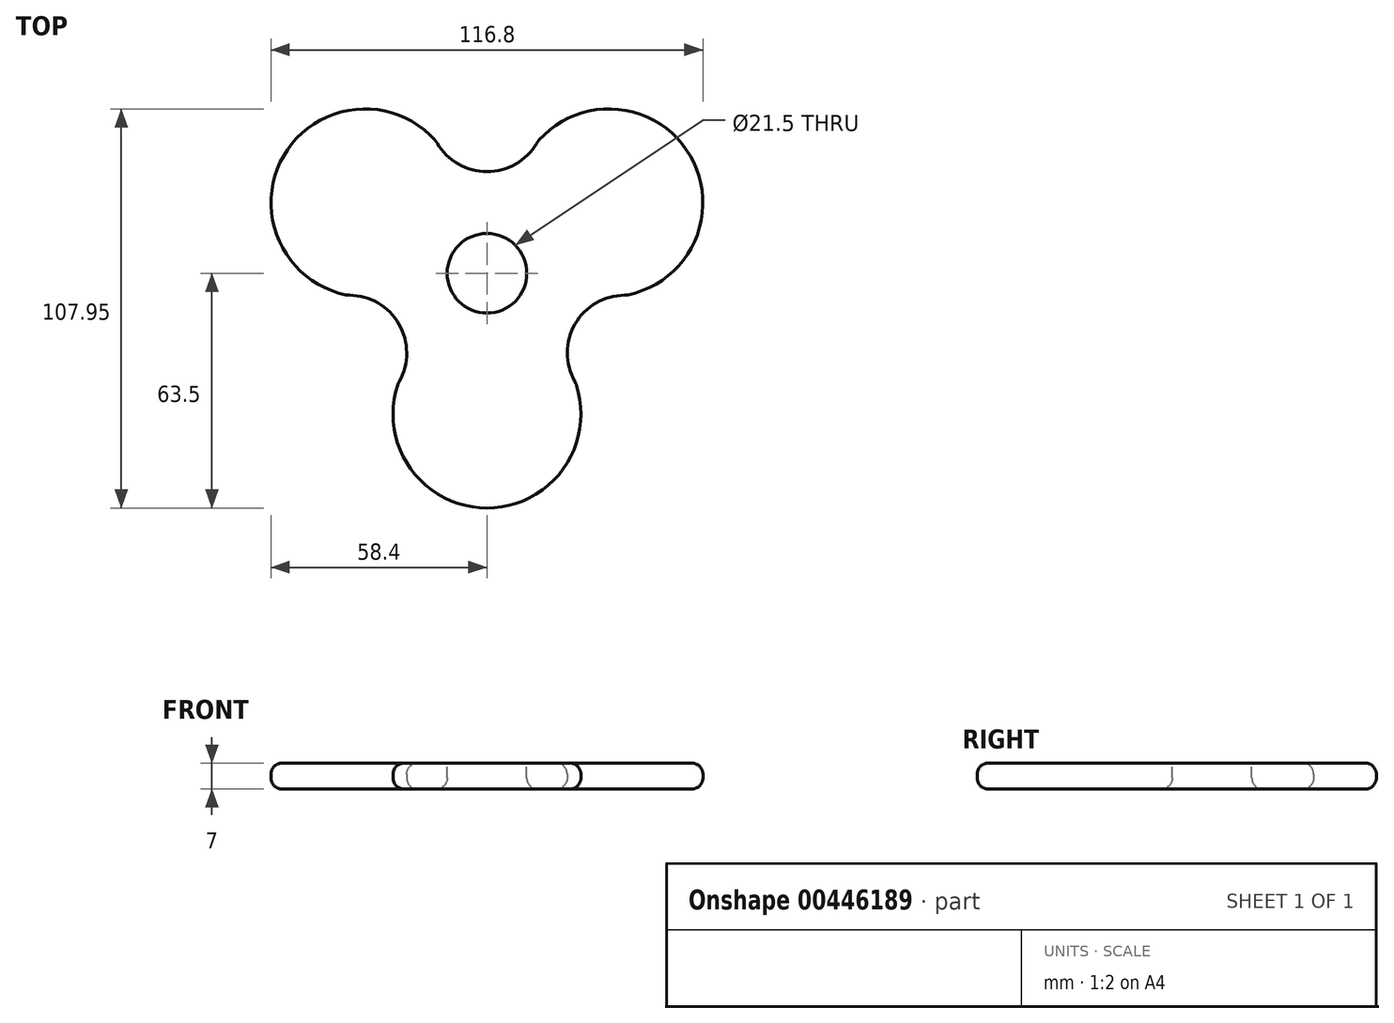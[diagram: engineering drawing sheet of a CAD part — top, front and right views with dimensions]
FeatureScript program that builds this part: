
annotation { "Feature Type Name" : "Feature", "Feature Type Description" : "" }
export const myFeature = defineFeature(function(context is Context, id is Id, definition is map)
    precondition{}
    {
        {
            var Q0;
            Q0=qCreatedBy(makeId("Top.planeOp"),FACE);
            var sketch = newSketch(context, id + "F0", { "sketchPlane" : qUnion([Q0])});
            skCircle(sketch, "E0", {"center": v(0, 0) * mm, "radius": 38.1 * mm});
            skCircle(sketch, "E1", {"center": v(0, -38.1) * mm, "radius": 25.4 * mm});
            skCircle(sketch, "E2", {"center": v(-33, 19.05) * mm, "radius": 25.4 * mm});
            skCircle(sketch, "E3", {"center": v(33, 19.05) * mm, "radius": 25.4 * mm});
            skArc(sketch, "E4", {"start": v(-23.95, -29.63) * mm, "mid": v(-23.81, -13.75) * mm, "end": v(-37.64, -5.93) * mm});
            skArc(sketch, "E5", {"start": v(37.64, -5.93) * mm, "mid": v(23.81, -13.75) * mm, "end": v(23.95, -29.63) * mm});
            skArc(sketch, "E6", {"start": v(-13.7, 35.55) * mm, "mid": v(0, 27.49) * mm, "end": v(13.7, 35.55) * mm});
            skSolve(sketch);
        }
        {
            var Q0;
            {var subQ1=sQuery(id+"F0.wireOp",EDGE,"E1");var subQ8=sQuery(id+"F0.wireOp",EDGE,"E5");var subQ11=makeQuery(id+"F0.imprint","INTERSECT",VERTEX,{"derivedFrom":[subQ1,subQ8]});Q0=makeQuery(id+"F0.imprint","IMPRINT",FACE,{"disambiguationData":[TD([[makeQuery(id+"F0.imprint","IMPRINT",EDGE,{"disambiguationData":[TD([[subQ11,-1.0]])],"derivedFrom":subQ1}),-1.0]])]});}
            var Q1;
            {var subQ1=sQuery(id+"F0.wireOp",EDGE,"E1");var subQ4=sQuery(id+"F0.wireOp",EDGE,"E5");var subQ7=makeQuery(id+"F0.imprint","INTERSECT",VERTEX,{"derivedFrom":[subQ1,subQ4]});Q1=makeQuery(id+"F0.imprint","IMPRINT",FACE,{"disambiguationData":[TD([[makeQuery(id+"F0.imprint","IMPRINT",EDGE,{"disambiguationData":[TD([[subQ7,-1.0]])],"derivedFrom":subQ1}),1.0]])]});}
            var Q2;
            {var subQ0=sQuery(id+"F0.wireOp",EDGE,"E1");var subQ1=sQuery(id+"F0.wireOp",EDGE,"E0");var subQ2=makeQuery(id+"F0.imprint","INTERSECT",VERTEX,{"derivedFrom":[subQ1,subQ0,sQuery(id+"F0.wireOp",EDGE,"E4")]});Q2=makeQuery(id+"F0.imprint","IMPRINT",FACE,{"disambiguationData":[TD([[makeQuery(id+"F0.imprint","IMPRINT",EDGE,{"disambiguationData":[TD([[subQ2,-1.0]])],"derivedFrom":subQ1}),-1.0]])]});}
            var Q3;
            {var subQ1=sQuery(id+"F0.wireOp",EDGE,"E3");var subQ4=sQuery(id+"F0.wireOp",EDGE,"E6");var subQ6=makeQuery(id+"F0.imprint","INTERSECT",VERTEX,{"derivedFrom":[subQ1,subQ4]});Q3=makeQuery(id+"F0.imprint","IMPRINT",FACE,{"disambiguationData":[TD([[makeQuery(id+"F0.imprint","IMPRINT",EDGE,{"disambiguationData":[TD([[subQ6,-1.0]])],"derivedFrom":subQ1}),1.0]])]});}
            var Q4;
            {var subQ0=sQuery(id+"F0.wireOp",EDGE,"E3");var subQ1=sQuery(id+"F0.wireOp",EDGE,"E0");var subQ2=makeQuery(id+"F0.imprint","INTERSECT",VERTEX,{"derivedFrom":[subQ1,subQ0,sQuery(id+"F0.wireOp",EDGE,"E5")]});Q4=makeQuery(id+"F0.imprint","IMPRINT",FACE,{"disambiguationData":[TD([[makeQuery(id+"F0.imprint","IMPRINT",EDGE,{"disambiguationData":[TD([[subQ2,-1.0]])],"derivedFrom":subQ1}),-1.0]])]});}
            var Q5;
            {var subQ1=sQuery(id+"F0.wireOp",EDGE,"E2");var subQ4=sQuery(id+"F0.wireOp",EDGE,"E6");var subQ6=makeQuery(id+"F0.imprint","INTERSECT",VERTEX,{"derivedFrom":[subQ1,subQ4]});Q5=makeQuery(id+"F0.imprint","IMPRINT",FACE,{"disambiguationData":[TD([[makeQuery(id+"F0.imprint","IMPRINT",EDGE,{"disambiguationData":[TD([[subQ6,1.0]])],"derivedFrom":subQ1}),1.0]])]});}
            var Q6;
            {var subQ0=sQuery(id+"F0.wireOp",EDGE,"E2");var subQ1=sQuery(id+"F0.wireOp",EDGE,"E0");var subQ2=makeQuery(id+"F0.imprint","INTERSECT",VERTEX,{"derivedFrom":[subQ1,subQ0,sQuery(id+"F0.wireOp",EDGE,"E4")]});Q6=makeQuery(id+"F0.imprint","IMPRINT",FACE,{"disambiguationData":[TD([[makeQuery(id+"F0.imprint","IMPRINT",EDGE,{"disambiguationData":[TD([[subQ2,1.0]])],"derivedFrom":subQ1}),-1.0]])]});}
            extrude(context, id + "F1", {"entities" : qUnion([Q0, Q1, Q2, Q3, Q4, Q5, Q6]), "endBound" : BoundingType.SYMMETRIC, "depth" : 7 * mm});
        }
        {
            var Q0;
            Q0=qCreatedBy(makeId("Top.planeOp"),FACE);
            var sketch = newSketch(context, id + "F2", { "sketchPlane" : qUnion([Q0])});
            skCircle(sketch, "E7", {"center": v(0, 0) * mm, "radius": 10.75 * mm});
            skSolve(sketch);
        }
        {
            var Q0;
            Q0 = qSketchRegion(id + "F2", true);
            extrude(context, id + "F3", {"entities" : qUnion([Q0]), "operationType" : NewBodyOperationType.REMOVE, "endBound" : BoundingType.SYMMETRIC, "oppositeDirection" : true, "depth" : 25 * mm});
        }
        {
            var Q0;
            Q0=makeQuery(id+"F1.opExtrude","CAP_EDGE",EDGE,{"disambiguationData":[OSD([sQuery(id+"F0.wireOp",EDGE,"E1")])],"isStart":false});
            var Q1;
            Q1=makeQuery(id+"F1.opExtrude","CAP_EDGE",EDGE,{"disambiguationData":[OSD([sQuery(id+"F0.wireOp",EDGE,"E5")])],"isStart":false});
            var Q2;
            Q2=makeQuery(id+"F1.opExtrude","CAP_EDGE",EDGE,{"disambiguationData":[OSD([sQuery(id+"F0.wireOp",EDGE,"E3")])],"isStart":false});
            var Q3;
            Q3=makeQuery(id+"F1.opExtrude","CAP_EDGE",EDGE,{"disambiguationData":[OSD([sQuery(id+"F0.wireOp",EDGE,"E6")])],"isStart":false});
            var Q4;
            Q4=makeQuery(id+"F1.opExtrude","CAP_EDGE",EDGE,{"disambiguationData":[OSD([sQuery(id+"F0.wireOp",EDGE,"E2")])],"isStart":false});
            var Q5;
            Q5=makeQuery(id+"F1.opExtrude","CAP_EDGE",EDGE,{"disambiguationData":[OSD([sQuery(id+"F0.wireOp",EDGE,"E4")])],"isStart":false});
            var Q6;
            Q6=makeQuery(id+"F1.opExtrude","CAP_FACE",FACE,{"disambiguationData":[OSD([sQuery(id+"F0.wireOp",EDGE,"E1"),sQuery(id+"F0.wireOp",EDGE,"E2"),sQuery(id+"F0.wireOp",EDGE,"E3"),sQuery(id+"F0.wireOp",EDGE,"E4"),sQuery(id+"F0.wireOp",EDGE,"E5"),sQuery(id+"F0.wireOp",EDGE,"E6")])],"isStart":true});
            fillet(context, id + "F4", {"entities" : qUnion([Q0, Q1, Q2, Q3, Q4, Q5, Q6]), "radius" : 3 * mm, "tangentPropagation" : true, "allowEdgeOverflow" : false});
        }
        {
            var Q0;
            Q0=makeQuery(id+"F4.opFillet","BLEND_EDGE",EDGE,{"blendedFrom":[makeQuery(id+"F1.opExtrude","CAP_EDGE",EDGE,{"disambiguationData":[OSD([sQuery(id+"F0.wireOp",EDGE,"E3")])],"isStart":false}),makeQuery(id+"F1.opExtrude","CAP_EDGE",EDGE,{"disambiguationData":[OSD([sQuery(id+"F0.wireOp",EDGE,"E5")])],"isStart":false})],"blendedInto":[]});
            var Q1;
            Q1=makeQuery(id+"F4.opFillet","BLEND_EDGE",EDGE,{"blendedFrom":[makeQuery(id+"F1.opExtrude","CAP_EDGE",EDGE,{"disambiguationData":[OSD([sQuery(id+"F0.wireOp",EDGE,"E3")])],"isStart":true}),makeQuery(id+"F1.opExtrude","CAP_EDGE",EDGE,{"disambiguationData":[OSD([sQuery(id+"F0.wireOp",EDGE,"E5")])],"isStart":true})],"blendedInto":[]});
            var Q2;
            Q2=makeQuery(id+"F1.opExtrude","SWEPT_EDGE",EDGE,{"disambiguationData":[OSD([sQuery(id+"F0.wireOp",EDGE,"E0"),sQuery(id+"F0.wireOp",EDGE,"E3"),sQuery(id+"F0.wireOp",EDGE,"E5")])]});
            var Q3;
            Q3=makeQuery(id+"F1.opExtrude","SWEPT_EDGE",EDGE,{"disambiguationData":[OSD([sQuery(id+"F0.wireOp",EDGE,"E0"),sQuery(id+"F0.wireOp",EDGE,"E3"),sQuery(id+"F0.wireOp",EDGE,"E6")])]});
            var Q4;
            Q4=makeQuery(id+"F4.opFillet","BLEND_EDGE",EDGE,{"blendedFrom":[makeQuery(id+"F1.opExtrude","CAP_EDGE",EDGE,{"disambiguationData":[OSD([sQuery(id+"F0.wireOp",EDGE,"E3")])],"isStart":true}),makeQuery(id+"F1.opExtrude","CAP_EDGE",EDGE,{"disambiguationData":[OSD([sQuery(id+"F0.wireOp",EDGE,"E6")])],"isStart":true})],"blendedInto":[]});
            var Q5;
            Q5=makeQuery(id+"F4.opFillet","BLEND_EDGE",EDGE,{"blendedFrom":[makeQuery(id+"F1.opExtrude","CAP_EDGE",EDGE,{"disambiguationData":[OSD([sQuery(id+"F0.wireOp",EDGE,"E3")])],"isStart":false}),makeQuery(id+"F1.opExtrude","CAP_EDGE",EDGE,{"disambiguationData":[OSD([sQuery(id+"F0.wireOp",EDGE,"E6")])],"isStart":false})],"blendedInto":[]});
            var Q6;
            Q6=makeQuery(id+"F1.opExtrude","SWEPT_EDGE",EDGE,{"disambiguationData":[OSD([sQuery(id+"F0.wireOp",EDGE,"E0"),sQuery(id+"F0.wireOp",EDGE,"E2"),sQuery(id+"F0.wireOp",EDGE,"E6")])]});
            var Q7;
            Q7=makeQuery(id+"F4.opFillet","BLEND_EDGE",EDGE,{"blendedFrom":[makeQuery(id+"F1.opExtrude","CAP_EDGE",EDGE,{"disambiguationData":[OSD([sQuery(id+"F0.wireOp",EDGE,"E2")])],"isStart":true}),makeQuery(id+"F1.opExtrude","CAP_EDGE",EDGE,{"disambiguationData":[OSD([sQuery(id+"F0.wireOp",EDGE,"E6")])],"isStart":true})],"blendedInto":[]});
            var Q8;
            Q8=makeQuery(id+"F4.opFillet","BLEND_EDGE",EDGE,{"blendedFrom":[makeQuery(id+"F1.opExtrude","CAP_EDGE",EDGE,{"disambiguationData":[OSD([sQuery(id+"F0.wireOp",EDGE,"E2")])],"isStart":false}),makeQuery(id+"F1.opExtrude","CAP_EDGE",EDGE,{"disambiguationData":[OSD([sQuery(id+"F0.wireOp",EDGE,"E6")])],"isStart":false})],"blendedInto":[]});
            var Q9;
            Q9=makeQuery(id+"F1.opExtrude","SWEPT_EDGE",EDGE,{"disambiguationData":[OSD([sQuery(id+"F0.wireOp",EDGE,"E0"),sQuery(id+"F0.wireOp",EDGE,"E2"),sQuery(id+"F0.wireOp",EDGE,"E4")])]});
            var Q10;
            Q10=makeQuery(id+"F4.opFillet","BLEND_EDGE",EDGE,{"blendedFrom":[makeQuery(id+"F1.opExtrude","CAP_EDGE",EDGE,{"disambiguationData":[OSD([sQuery(id+"F0.wireOp",EDGE,"E2")])],"isStart":true}),makeQuery(id+"F1.opExtrude","CAP_EDGE",EDGE,{"disambiguationData":[OSD([sQuery(id+"F0.wireOp",EDGE,"E4")])],"isStart":true})],"blendedInto":[]});
            var Q11;
            Q11=makeQuery(id+"F4.opFillet","BLEND_EDGE",EDGE,{"blendedFrom":[makeQuery(id+"F1.opExtrude","CAP_EDGE",EDGE,{"disambiguationData":[OSD([sQuery(id+"F0.wireOp",EDGE,"E2")])],"isStart":false}),makeQuery(id+"F1.opExtrude","CAP_EDGE",EDGE,{"disambiguationData":[OSD([sQuery(id+"F0.wireOp",EDGE,"E4")])],"isStart":false})],"blendedInto":[]});
            var Q12;
            Q12=makeQuery(id+"F1.opExtrude","SWEPT_EDGE",EDGE,{"disambiguationData":[OSD([sQuery(id+"F0.wireOp",EDGE,"E0"),sQuery(id+"F0.wireOp",EDGE,"E1"),sQuery(id+"F0.wireOp",EDGE,"E4")])]});
            var Q13;
            Q13=makeQuery(id+"F4.opFillet","BLEND_EDGE",EDGE,{"blendedFrom":[makeQuery(id+"F1.opExtrude","CAP_EDGE",EDGE,{"disambiguationData":[OSD([sQuery(id+"F0.wireOp",EDGE,"E1")])],"isStart":false}),makeQuery(id+"F1.opExtrude","CAP_EDGE",EDGE,{"disambiguationData":[OSD([sQuery(id+"F0.wireOp",EDGE,"E4")])],"isStart":false})],"blendedInto":[]});
            var Q14;
            Q14=makeQuery(id+"F4.opFillet","BLEND_EDGE",EDGE,{"blendedFrom":[makeQuery(id+"F1.opExtrude","CAP_EDGE",EDGE,{"disambiguationData":[OSD([sQuery(id+"F0.wireOp",EDGE,"E1")])],"isStart":true}),makeQuery(id+"F1.opExtrude","CAP_EDGE",EDGE,{"disambiguationData":[OSD([sQuery(id+"F0.wireOp",EDGE,"E4")])],"isStart":true})],"blendedInto":[]});
            var Q15;
            Q15=makeQuery(id+"F1.opExtrude","SWEPT_EDGE",EDGE,{"disambiguationData":[OSD([sQuery(id+"F0.wireOp",EDGE,"E0"),sQuery(id+"F0.wireOp",EDGE,"E1"),sQuery(id+"F0.wireOp",EDGE,"E5")])]});
            var Q16;
            Q16=makeQuery(id+"F4.opFillet","BLEND_EDGE",EDGE,{"blendedFrom":[makeQuery(id+"F1.opExtrude","CAP_EDGE",EDGE,{"disambiguationData":[OSD([sQuery(id+"F0.wireOp",EDGE,"E1")])],"isStart":true}),makeQuery(id+"F1.opExtrude","CAP_EDGE",EDGE,{"disambiguationData":[OSD([sQuery(id+"F0.wireOp",EDGE,"E5")])],"isStart":true})],"blendedInto":[]});
            var Q17;
            Q17=makeQuery(id+"F4.opFillet","BLEND_EDGE",EDGE,{"blendedFrom":[makeQuery(id+"F1.opExtrude","CAP_EDGE",EDGE,{"disambiguationData":[OSD([sQuery(id+"F0.wireOp",EDGE,"E1")])],"isStart":false}),makeQuery(id+"F1.opExtrude","CAP_EDGE",EDGE,{"disambiguationData":[OSD([sQuery(id+"F0.wireOp",EDGE,"E5")])],"isStart":false})],"blendedInto":[]});
            fillet(context, id + "F5", {"entities" : qUnion([Q0, Q1, Q2, Q3, Q4, Q5, Q6, Q7, Q8, Q9, Q10, Q11, Q12, Q13, Q14, Q15, Q16, Q17]), "radius" : 5 * mm, "tangentPropagation" : true, "allowEdgeOverflow" : false});
        }
    });
